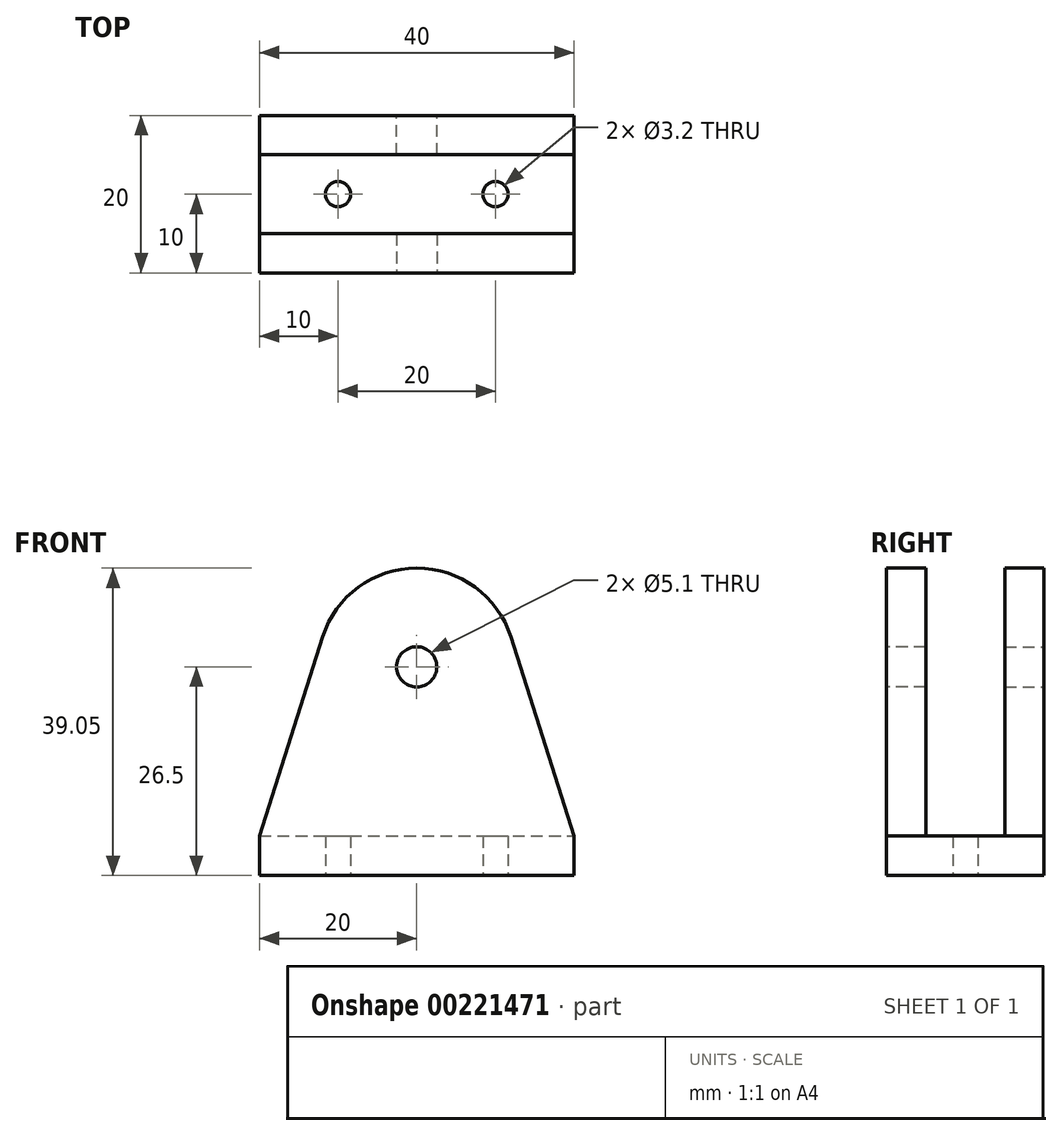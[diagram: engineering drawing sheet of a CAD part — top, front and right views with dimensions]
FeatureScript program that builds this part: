
annotation { "Feature Type Name" : "Feature", "Feature Type Description" : "" }
export const myFeature = defineFeature(function(context is Context, id is Id, definition is map)
    precondition{}
    {
        {
            var Q0;
            Q0=qCreatedBy(makeId("Front.planeOp"),FACE);
            var sketch = newSketch(context, id + "F3", { "sketchPlane" : qUnion([Q0])});
            skLineSegment(sketch, "E0.bottom", {"start": v(0, 0) * mm, "end": v(40, 0) * mm});
            skLineSegment(sketch, "E0.left", {"start": v(0, 0) * mm, "end": v(0, 5) * mm});
            skLineSegment(sketch, "E0.right", {"start": v(40, 0) * mm, "end": v(40, 5) * mm});
            skCircle(sketch, "E1", {"center": v(20, 26.5) * mm, "radius": 2.55 * mm});
            skArc(sketch, "E2.0", {"start": v(31.96, 30.3) * mm, "mid": v(20, 39.05) * mm, "end": v(8.04, 30.3) * mm});
            skLineSegment(sketch, "E3", {"start": v(0, 5) * mm, "end": v(8.04, 30.3) * mm});
            skLineSegment(sketch, "E4", {"start": v(40, 5) * mm, "end": v(31.96, 30.3) * mm});
            skPoint(sketch, "E5", {"position": v(20, 0) * mm});
            skSolve(sketch);
        }
        {
            var Q0;
            Q0=makeQuery(id+"F3.imprint","IMPRINT",FACE,{"disambiguationData":[TD([[makeQuery(id+"F3.imprint","IMPRINT",EDGE,{"derivedFrom":sQuery(id+"F3.wireOp",EDGE,"E0.bottom")}),1.0]])]});
            extrude(context, id + "F4", {"entities" : qUnion([Q0]), "depth" : 5 * mm});
        }
        {
            var Q0;
            Q0=makeQuery(id+"F4.opExtrude","CAP_FACE",FACE,{"disambiguationData":[OSD([sQuery(id+"F3.wireOp",EDGE,"E0.bottom"),sQuery(id+"F3.wireOp",EDGE,"E0.left"),sQuery(id+"F3.wireOp",EDGE,"E0.right"),sQuery(id+"F3.wireOp",EDGE,"E1"),sQuery(id+"F3.wireOp",EDGE,"E2.0"),sQuery(id+"F3.wireOp",EDGE,"E3"),sQuery(id+"F3.wireOp",EDGE,"E4")])],"isStart":false});
            var sketch = newSketch(context, id + "F0", { "sketchPlane" : qUnion([Q0])});
            skLineSegment(sketch, "E6.bottom", {"start": v(0, 0) * mm, "end": v(40, 0) * mm});
            skLineSegment(sketch, "E6.top", {"start": v(0, 5) * mm, "end": v(40, 5) * mm});
            skLineSegment(sketch, "E6.left", {"start": v(0, 0) * mm, "end": v(0, 5) * mm});
            skLineSegment(sketch, "E6.right", {"start": v(40, 0) * mm, "end": v(40, 5) * mm});
            skSolve(sketch);
        }
        {
            var Q0;
            Q0=makeQuery(id+"F0.imprint","IMPRINT",FACE,{"disambiguationData":[TD([[makeQuery(id+"F0.imprint","IMPRINT",EDGE,{"derivedFrom":sQuery(id+"F0.wireOp",EDGE,"E6.bottom")}),1.0]])]});
            extrude(context, id + "F5", {"entities" : qUnion([Q0]), "operationType" : NewBodyOperationType.ADD, "depth" : 5 * mm});
        }
        {
            var Q0;
            Q0=makeQuery(id+"F4.opExtrude","SWEPT_BODY",BODY,{"disambiguationData":[OSD([sQuery(id+"F3.wireOp",EDGE,"E0.bottom"),sQuery(id+"F3.wireOp",EDGE,"E0.left"),sQuery(id+"F3.wireOp",EDGE,"E0.right"),sQuery(id+"F3.wireOp",EDGE,"E1"),sQuery(id+"F3.wireOp",EDGE,"E2.0"),sQuery(id+"F3.wireOp",EDGE,"E3"),sQuery(id+"F3.wireOp",EDGE,"E4")])]});
            var Q1;
            Q1=makeQuery(id+"F5.opExtrude","CAP_FACE",FACE,{"disambiguationData":[OSD([sQuery(id+"F0.wireOp",EDGE,"E6.bottom"),sQuery(id+"F0.wireOp",EDGE,"E6.top"),sQuery(id+"F0.wireOp",EDGE,"E6.left"),sQuery(id+"F0.wireOp",EDGE,"E6.right")])],"isStart":false});
            mirror(context, id + "F1", {"operationType" : NewBodyOperationType.ADD, "entities" : qUnion([Q0]), "mirrorPlane" : qUnion([Q1])});
        }
        {
            var Q0;
            {var subQ0=makeQuery(id+"F5.opExtrude","SWEPT_FACE",FACE,{"disambiguationData":[OSD([sQuery(id+"F0.wireOp",EDGE,"E6.top")])]});Q0=makeQuery(id+"F1.boolean.opBoolean","MERGE",FACE,{"derivedFrom":[subQ0,makeQuery(id+"F1.opPattern","COPY",FACE,{"derivedFrom":subQ0,"instanceName":"1"})]});}
            var sketch = newSketch(context, id + "F2", { "sketchPlane" : qUnion([Q0])});
            skPoint(sketch, "E7", {"position": v(10, -10) * mm});
            skPoint(sketch, "E8", {"position": v(30, -10) * mm});
            skLineSegment(sketch, "E9", {"start": v(0, -10) * mm, "end": v(40, -10) * mm, "construction": true});
            skSolve(sketch);
        }
        {
            var Q0;
            Q0=sQuery(id+"F2.wireOp",VERTEX,"E7");
            var Q1;
            Q1=sQuery(id+"F2.wireOp",VERTEX,"E8");
            var Q2;
            Q2=makeQuery(id+"F4.opExtrude","SWEPT_BODY",BODY,{"disambiguationData":[OSD([sQuery(id+"F3.wireOp",EDGE,"E0.bottom"),sQuery(id+"F3.wireOp",EDGE,"E0.left"),sQuery(id+"F3.wireOp",EDGE,"E0.right"),sQuery(id+"F3.wireOp",EDGE,"E1"),sQuery(id+"F3.wireOp",EDGE,"E2.0"),sQuery(id+"F3.wireOp",EDGE,"E3"),sQuery(id+"F3.wireOp",EDGE,"E4")])]});
            hole(context, id + "F6", {"style" : HoleStyle.SIMPLE, "endStyle" : HoleEndStyle.THROUGH, "standardTappedOrClearance" : lookupTablePath({ "standard" : "ISO", "size" : "M3" }), "standardBlindInLast" : lookupTablePath({ "standard" : "ISO", "size" : "M3" }), "holeDiameter" : 3.2 * mm, "locations" : qUnion([Q0, Q1]), "scope" : qUnion([Q2]), "isTappedThrough" : true});
        }
    });
